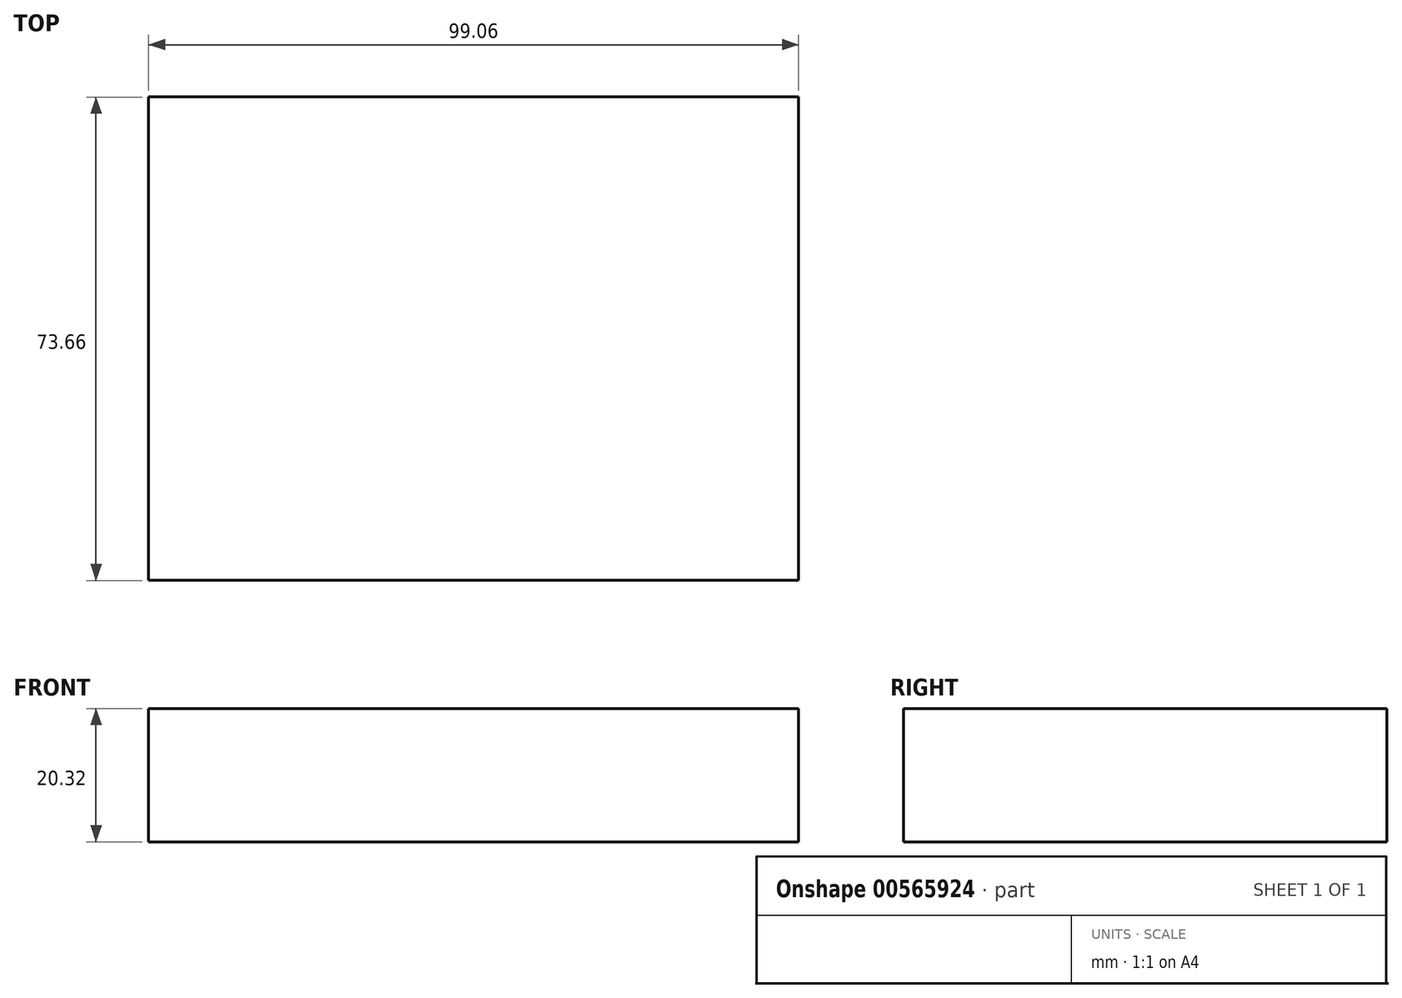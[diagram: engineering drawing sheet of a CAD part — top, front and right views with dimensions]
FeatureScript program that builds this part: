
annotation { "Feature Type Name" : "Feature", "Feature Type Description" : "" }
export const myFeature = defineFeature(function(context is Context, id is Id, definition is map)
    precondition{}
    {
        {
            var Q0;
            Q0=qCreatedBy(makeId("Top.planeOp"),FACE);
            var sketch = newSketch(context, id + "F0", { "sketchPlane" : qUnion([Q0])});
            skLineSegment(sketch, "E0", {"start": v(-57.76, 48.9) * mm, "end": v(-57.76, -24.77) * mm});
            skLineSegment(sketch, "E1", {"start": v(-57.76, -24.77) * mm, "end": v(41.3, -24.77) * mm});
            skLineSegment(sketch, "E2", {"start": v(41.3, -24.77) * mm, "end": v(41.3, 48.9) * mm});
            skLineSegment(sketch, "E3", {"start": v(41.3, 48.9) * mm, "end": v(-57.76, 48.9) * mm});
            skSolve(sketch);
        }
        {
            var Q0;
            Q0=makeQuery(id+"F0.imprint","IMPRINT",FACE,{"disambiguationData":[TD([[makeQuery(id+"F0.imprint","IMPRINT",EDGE,{"derivedFrom":sQuery(id+"F0.wireOp",EDGE,"E0")}),1.0]])]});
            extrude(context, id + "F1", {"entities" : qUnion([Q0]), "depth" : 20.32 * mm, "offsetDistance" : 25.4 * mm});
        }
    });
